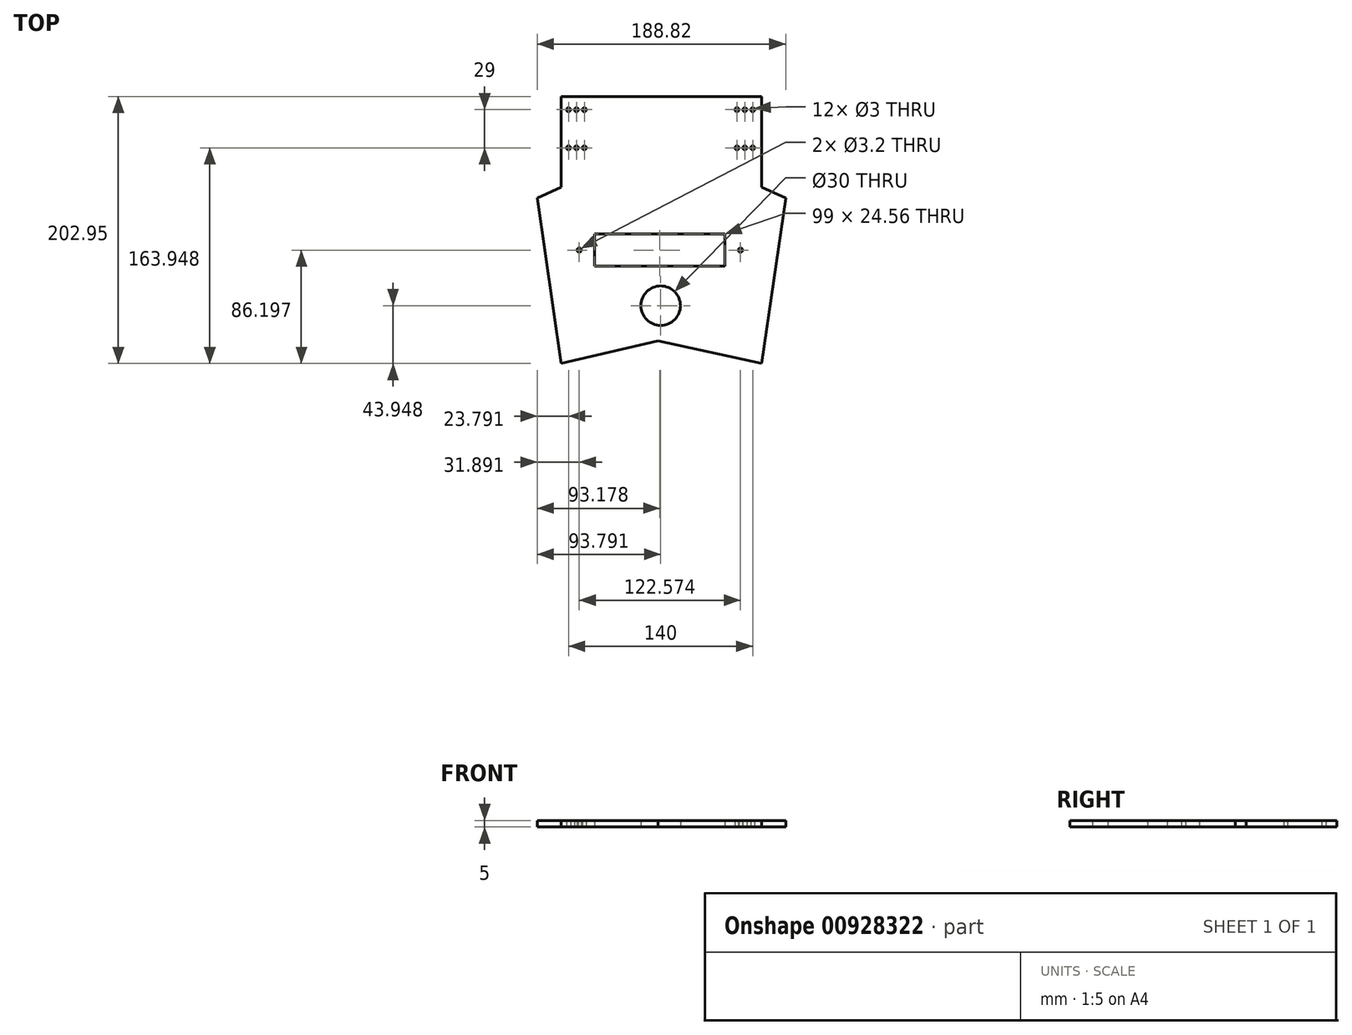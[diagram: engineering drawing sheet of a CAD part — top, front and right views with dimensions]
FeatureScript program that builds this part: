
annotation { "Feature Type Name" : "Feature", "Feature Type Description" : "" }
export const myFeature = defineFeature(function(context is Context, id is Id, definition is map)
    precondition{}
    {
        {
            var Q0;
            Q0=qCreatedBy(makeId("Top.planeOp"),FACE);
            var sketch = newSketch(context, id + "F0", { "sketchPlane" : qUnion([Q0])});
            skCircle(sketch, "E0", {"center": v(-398.19, 512.83) * mm, "radius": 1.5 * mm});
            skCircle(sketch, "E1.0.1.0", {"center": v(-398.19, 541.83) * mm, "radius": 1.5 * mm});
            skCircle(sketch, "E1.1.0.0", {"center": v(-392.19, 512.83) * mm, "radius": 1.5 * mm});
            skCircle(sketch, "E1.1.1.0", {"center": v(-392.19, 541.83) * mm, "radius": 1.5 * mm});
            skCircle(sketch, "E1.2.0.0", {"center": v(-386.19, 512.83) * mm, "radius": 1.5 * mm});
            skCircle(sketch, "E1.2.1.0", {"center": v(-386.19, 541.83) * mm, "radius": 1.5 * mm});
            skLineSegment(sketch, "E1.direction1", {"start": v(-398.19, 512.83) * mm, "end": v(-392.19, 512.83) * mm, "construction": true});
            skLineSegment(sketch, "E1.direction2", {"start": v(-398.19, 512.83) * mm, "end": v(-398.19, 541.83) * mm, "construction": true});
            skLineSegment(sketch, "E2", {"start": v(-328.19, 515.84) * mm, "end": v(-328.19, 543.63) * mm});
            skCircle(sketch, "E3.MirrorC", {"center": v(-258.19, 541.83) * mm, "radius": 1.5 * mm});
            skLineSegment(sketch, "E4.MirrorCS", {"start": v(-258.19, 512.83) * mm, "end": v(-264.19, 512.83) * mm, "construction": true});
            skCircle(sketch, "E5.MirrorC", {"center": v(-270.19, 512.83) * mm, "radius": 1.5 * mm});
            skCircle(sketch, "E6.MirrorC", {"center": v(-258.19, 512.83) * mm, "radius": 1.5 * mm});
            skCircle(sketch, "E7.MirrorC", {"center": v(-264.19, 512.83) * mm, "radius": 1.5 * mm});
            skCircle(sketch, "E8.MirrorC", {"center": v(-264.19, 541.83) * mm, "radius": 1.5 * mm});
            skCircle(sketch, "E9.MirrorC", {"center": v(-270.19, 541.83) * mm, "radius": 1.5 * mm});
            skLineSegment(sketch, "E10.MirrorCS", {"start": v(-258.19, 512.83) * mm, "end": v(-258.19, 541.83) * mm, "construction": true});
            skLineSegment(sketch, "E11.bottom", {"start": v(-403.72, 551.83) * mm, "end": v(-251.43, 551.83) * mm});
            skLineSegment(sketch, "E11.top", {"start": v(-403.72, 348.88) * mm, "end": v(-251.43, 348.88) * mm});
            skLineSegment(sketch, "E11.left", {"start": v(-403.72, 551.83) * mm, "end": v(-403.72, 348.88) * mm});
            skLineSegment(sketch, "E11.right", {"start": v(-251.43, 551.83) * mm, "end": v(-251.43, 348.88) * mm});
            skPoint(sketch, "E12", {"position": v(-397.65, 551.83) * mm});
            skCircle(sketch, "E13", {"center": v(-328.19, 392.83) * mm, "radius": 15 * mm});
            skLineSegment(sketch, "E14", {"start": v(-403.72, 482.83) * mm, "end": v(-421.98, 474.68) * mm});
            skLineSegment(sketch, "E15", {"start": v(-251.43, 482.83) * mm, "end": v(-233.16, 474.68) * mm});
            skLineSegment(sketch, "E16", {"start": v(-394.09, 435.08) * mm, "end": v(-378.3, 447.36) * mm});
            skLineSegment(sketch, "E17", {"start": v(-378.3, 447.36) * mm, "end": v(-279.3, 447.36) * mm});
            skLineSegment(sketch, "E18", {"start": v(-279.3, 447.36) * mm, "end": v(-263.52, 435.08) * mm});
            skLineSegment(sketch, "E19", {"start": v(-263.52, 435.08) * mm, "end": v(-279.3, 422.8) * mm});
            skLineSegment(sketch, "E20", {"start": v(-279.3, 422.8) * mm, "end": v(-378.3, 422.8) * mm});
            skLineSegment(sketch, "E21", {"start": v(-378.3, 422.8) * mm, "end": v(-394.09, 435.08) * mm});
            skLineSegment(sketch, "E22", {"start": v(-378.3, 447.36) * mm, "end": v(-378.3, 422.8) * mm});
            skLineSegment(sketch, "E23", {"start": v(-279.3, 447.36) * mm, "end": v(-279.3, 422.8) * mm});
            skCircle(sketch, "E24", {"center": v(-390.09, 435.08) * mm, "radius": 1.6 * mm});
            skCircle(sketch, "E25", {"center": v(-267.52, 435.08) * mm, "radius": 1.6 * mm});
            skLineSegment(sketch, "E26", {"start": v(-328.19, 392.83) * mm, "end": v(-280.65, 392.83) * mm});
            skLineSegment(sketch, "E27", {"start": v(-421.98, 474.68) * mm, "end": v(-403.72, 348.88) * mm});
            skLineSegment(sketch, "E28", {"start": v(-233.16, 474.68) * mm, "end": v(-251.43, 348.88) * mm});
            skLineSegment(sketch, "E29", {"start": v(-394.83, 341.52) * mm, "end": v(-258.6, 341.52) * mm});
            skLineSegment(sketch, "E30", {"start": v(-258.6, 341.52) * mm, "end": v(-251.43, 348.88) * mm});
            skLineSegment(sketch, "E31", {"start": v(-403.72, 348.88) * mm, "end": v(-394.83, 341.52) * mm});
            skLineSegment(sketch, "E32.bottom", {"start": v(-393.22, 348.99) * mm, "end": v(-259.35, 348.99) * mm});
            skLineSegment(sketch, "E32.top", {"start": v(-393.22, 346.62) * mm, "end": v(-259.35, 346.62) * mm});
            skLineSegment(sketch, "E32.left", {"start": v(-393.22, 348.99) * mm, "end": v(-393.22, 346.62) * mm});
            skLineSegment(sketch, "E32.right", {"start": v(-259.35, 348.99) * mm, "end": v(-259.35, 346.62) * mm});
            skLineSegment(sketch, "E33", {"start": v(-403.72, 348.88) * mm, "end": v(-328.74, 366.29) * mm});
            skLineSegment(sketch, "E34", {"start": v(-331.6, 366.29) * mm, "end": v(-251.43, 348.88) * mm});
            skLineSegment(sketch, "E35", {"start": v(-394.83, 341.52) * mm, "end": v(-403.72, 336.93) * mm});
            skLineSegment(sketch, "E36", {"start": v(-403.72, 336.93) * mm, "end": v(-403.72, 348.88) * mm});
            skLineSegment(sketch, "E37", {"start": v(-258.6, 341.52) * mm, "end": v(-251.43, 334.54) * mm});
            skLineSegment(sketch, "E38", {"start": v(-251.43, 348.88) * mm, "end": v(-251.43, 334.54) * mm});
            skSolve(sketch);
        }
        {
            var Q0;
            {var subQ2=sQuery(id+"F0.wireOp",EDGE,"E14");Q0=makeQuery(id+"F0.imprint","IMPRINT",FACE,{"disambiguationData":[TD([[makeQuery(id+"F0.imprint","IMPRINT",EDGE,{"derivedFrom":subQ2}),1.0]])]});}
            var Q1;
            {var subQ2=sQuery(id+"F0.wireOp",EDGE,"E15");Q1=makeQuery(id+"F0.imprint","IMPRINT",FACE,{"disambiguationData":[TD([[makeQuery(id+"F0.imprint","IMPRINT",EDGE,{"derivedFrom":subQ2}),-1.0]])]});}
            var Q2;
            Q2=makeQuery(id+"F0.imprint","IMPRINT",FACE,{"disambiguationData":[TD([[makeQuery(id+"F0.imprint","IMPRINT",EDGE,{"derivedFrom":sQuery(id+"F0.wireOp",EDGE,"E0")}),-1.0]])]});
            var Q3;
            Q3=makeQuery(id+"F0.imprint","IMPRINT",FACE,{"disambiguationData":[TD([[makeQuery(id+"F0.imprint","IMPRINT",EDGE,{"derivedFrom":sQuery(id+"F0.wireOp",EDGE,"E16")}),-1.0]])]});
            var Q4;
            Q4=makeQuery(id+"F0.imprint","IMPRINT",FACE,{"disambiguationData":[TD([[makeQuery(id+"F0.imprint","IMPRINT",EDGE,{"derivedFrom":sQuery(id+"F0.wireOp",EDGE,"E18")}),-1.0]])]});
            extrude(context, id + "F1", {"entities" : qUnion([Q0, Q1, Q2, Q3, Q4]), "depth" : 5 * mm, "offsetDistance" : 25 * mm});
        }
    });
